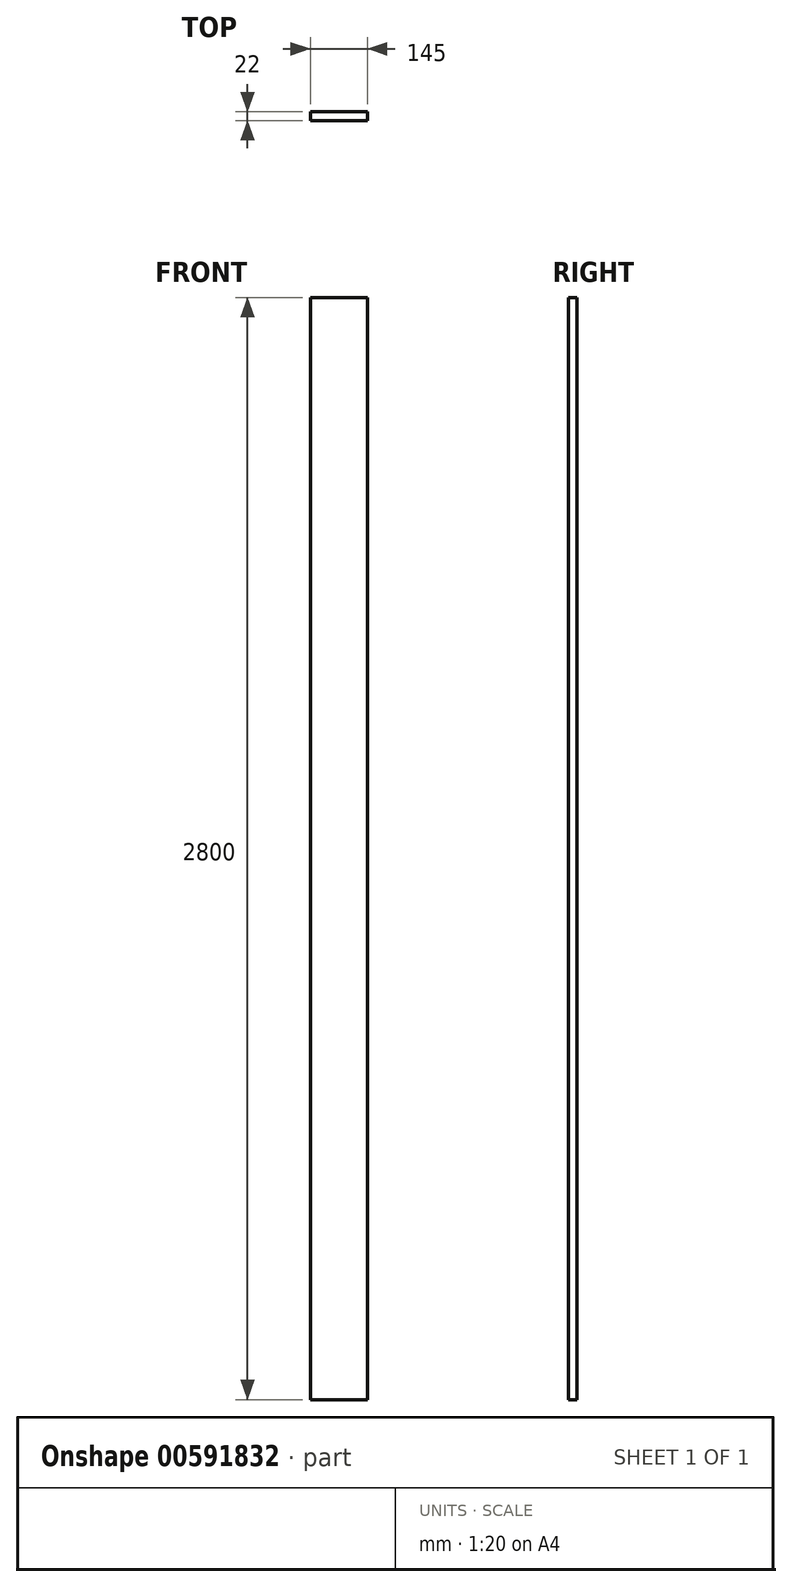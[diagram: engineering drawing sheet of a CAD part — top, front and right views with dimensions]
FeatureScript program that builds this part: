
annotation { "Feature Type Name" : "Feature", "Feature Type Description" : "" }
export const myFeature = defineFeature(function(context is Context, id is Id, definition is map)
    precondition{}
    {
        {
            var Q0;
            Q0=qCreatedBy(makeId("Top.planeOp"),FACE);
            var sketch = newSketch(context, id + "F0", { "sketchPlane" : qUnion([Q0])});
            skLineSegment(sketch, "E0.bottom", {"start": v(0, 0) * mm, "end": v(145, 0) * mm});
            skLineSegment(sketch, "E0.top", {"start": v(0, 22) * mm, "end": v(145, 22) * mm});
            skLineSegment(sketch, "E0.left", {"start": v(0, 0) * mm, "end": v(0, 22) * mm});
            skLineSegment(sketch, "E0.right", {"start": v(145, 0) * mm, "end": v(145, 22) * mm});
            skSolve(sketch);
        }
        {
            var Q0;
            Q0=makeQuery(id+"F0.imprint","IMPRINT",FACE,{"disambiguationData":[TD([[makeQuery(id+"F0.imprint","IMPRINT",EDGE,{"derivedFrom":sQuery(id+"F0.wireOp",EDGE,"E0.bottom")}),1.0]])]});
            extrude(context, id + "F1", {"entities" : qUnion([Q0]), "depth" : (2800) * mm, "offsetDistance" : 25 * mm});
        }
    });
